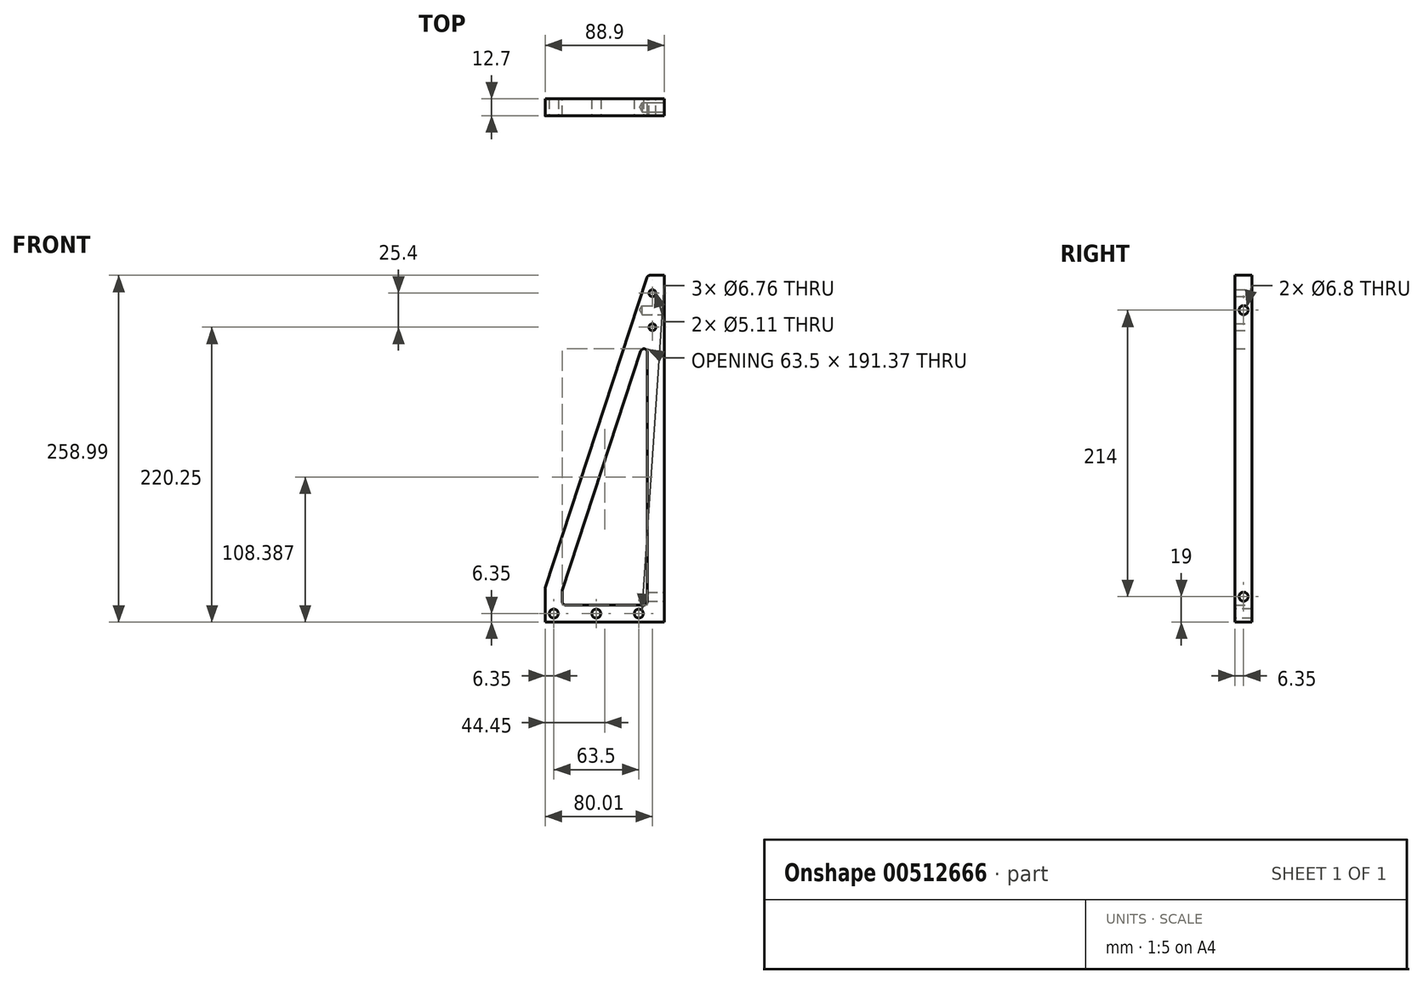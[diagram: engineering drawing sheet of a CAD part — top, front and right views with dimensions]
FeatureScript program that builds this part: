
annotation { "Feature Type Name" : "Feature", "Feature Type Description" : "" }
export const myFeature = defineFeature(function(context is Context, id is Id, definition is map)
    precondition{}
    {
        {
            var Q0;
            Q0=qCreatedBy(makeId("Front.planeOp"),FACE);
            var sketch = newSketch(context, id + "F0", { "sketchPlane" : qUnion([Q0])});
            skLineSegment(sketch, "E0", {"start": v(0, 0) * mm, "end": v(88.9, 0) * mm});
            skLineSegment(sketch, "E1", {"start": v(0, 0) * mm, "end": v(0, 25.4) * mm});
            skLineSegment(sketch, "E2", {"start": v(0, 25.4) * mm, "end": v(74.12, 252) * mm});
            skPoint(sketch, "E3.endSnap0", {"position": v(0, 12.7) * mm});
            skLineSegment(sketch, "E4", {"start": v(12.7, 23.38) * mm, "end": v(12.7, 12.7) * mm});
            skLineSegment(sketch, "E5", {"start": v(88.9, 0) * mm, "end": v(88.9, 252) * mm});
            skLineSegment(sketch, "E6", {"start": v(88.9, 252) * mm, "end": v(74.12, 252) * mm});
            skLineSegment(sketch, "E7", {"start": v(88.9, 252) * mm, "end": v(88.9, 239.3) * mm});
            skLineSegment(sketch, "E8", {"start": v(88.9, 239.3) * mm, "end": v(88.9, 226.6) * mm});
            skLineSegment(sketch, "E9", {"start": v(88.9, 0) * mm, "end": v(88.9, 12.7) * mm});
            skLineSegment(sketch, "E10", {"start": v(88.9, 12.7) * mm, "end": v(12.7, 12.7) * mm});
            skLineSegment(sketch, "E11", {"start": v(70.53, 30.21) * mm, "end": v(72.74, 26.95) * mm});
            skLineSegment(sketch, "E12", {"start": v(88.9, 12.7) * mm, "end": v(76.2, 12.7) * mm});
            skLineSegment(sketch, "E13", {"start": v(76.2, 12.7) * mm, "end": v(76.2, 217.5) * mm});
            skLineSegment(sketch, "E14", {"start": v(12.7, 23.38) * mm, "end": v(76.2, 217.5) * mm});
            skPoint(sketch, "E15.orphan", {"position": v(12.7, 25.4) * mm});
            skLineSegment(sketch, "E16", {"start": v(74.12, 252) * mm, "end": v(76.4, 258.99) * mm});
            skLineSegment(sketch, "E17", {"start": v(88.9, 252) * mm, "end": v(88.9, 258.99) * mm});
            skLineSegment(sketch, "E18", {"start": v(88.9, 258.99) * mm, "end": v(76.4, 258.99) * mm});
            skSolve(sketch);
        }
        {
            var Q0;
            Q0=makeQuery(id+"F0.imprint","IMPRINT",FACE,{"disambiguationData":[TD([[makeQuery(id+"F0.imprint","IMPRINT",EDGE,{"derivedFrom":sQuery(id+"F0.wireOp",EDGE,"E0")}),1.0]])]});
            var Q1;
            Q1=makeQuery(id+"F0.imprint","IMPRINT",FACE,{"disambiguationData":[TD([[makeQuery(id+"F0.imprint","IMPRINT",EDGE,{"derivedFrom":sQuery(id+"F0.wireOp",EDGE,"E6")}),-1.0]])]});
            extrude(context, id + "F1", {"entities" : qUnion([Q0, Q1]), "depth" : 12.7 * mm});
        }
        {
            var Q0;
            Q0=makeQuery(id+"F1.opExtrude","SWEPT_EDGE",EDGE,{"disambiguationData":[OSD([sQuery(id+"F0.wireOp",EDGE,"E2"),sQuery(id+"F0.wireOp",EDGE,"E6")])]});
            var Q1;
            Q1=makeQuery(id+"F1.opExtrude","SWEPT_EDGE",EDGE,{"disambiguationData":[OSD([sQuery(id+"F0.wireOp",EDGE,"E1"),sQuery(id+"F0.wireOp",EDGE,"E2")])]});
            var Q2;
            Q2=makeQuery(id+"F1.opExtrude","SWEPT_EDGE",EDGE,{"disambiguationData":[OSD([sQuery(id+"F0.wireOp",EDGE,"E10"),sQuery(id+"F0.wireOp",EDGE,"E13")])]});
            var Q3;
            Q3=makeQuery(id+"F1.opExtrude","SWEPT_EDGE",EDGE,{"disambiguationData":[OSD([sQuery(id+"F0.wireOp",EDGE,"E4"),sQuery(id+"F0.wireOp",EDGE,"E10")])]});
            var Q4;
            Q4=makeQuery(id+"F1.opExtrude","SWEPT_EDGE",EDGE,{"disambiguationData":[OSD([sQuery(id+"F0.wireOp",EDGE,"E4"),sQuery(id+"F0.wireOp",EDGE,"E14")])]});
            var Q5;
            Q5=makeQuery(id+"F1.opExtrude","SWEPT_EDGE",EDGE,{"disambiguationData":[OSD([sQuery(id+"F0.wireOp",EDGE,"E13"),sQuery(id+"F0.wireOp",EDGE,"E14")])]});
            var Q6;
            Q6=makeQuery(id+"F1.opExtrude","SWEPT_EDGE",EDGE,{"disambiguationData":[OSD([sQuery(id+"F0.wireOp",EDGE,"E16"),sQuery(id+"F0.wireOp",EDGE,"E18")])]});
            fillet(context, id + "F2", {"entities" : qUnion([Q0, Q1, Q2, Q3, Q4, Q5, Q6]), "radius" : 2.54 * mm, "tangentPropagation" : true, "allowEdgeOverflow" : false});
        }
        {
            var Q0;
            Q0=makeQuery(id+"F1.opExtrude","SWEPT_FACE",FACE,{"disambiguationData":[OSD([sQuery(id+"F0.wireOp",EDGE,"E5"),sQuery(id+"F0.wireOp",EDGE,"E7"),sQuery(id+"F0.wireOp",EDGE,"E8"),sQuery(id+"F0.wireOp",EDGE,"E9")])]});
            var sketch = newSketch(context, id + "F3", { "sketchPlane" : qUnion([Q0])});
            skLineSegment(sketch, "E19", {"start": v(-6.35, 0) * mm, "end": v(-6.35, 19) * mm});
            skLineSegment(sketch, "E20", {"start": v(-6.35, 19) * mm, "end": v(-6.35, 233) * mm});
            skSolve(sketch);
        }
        {
            var Q0;
            Q0=sQuery(id+"F3.wireOp",VERTEX,"E20.end");
            var Q1;
            Q1=sQuery(id+"F3.wireOp",VERTEX,"E20.start");
            var Q2;
            Q2=makeQuery(id+"F1.opExtrude","SWEPT_BODY",BODY,{"disambiguationData":[OSD([sQuery(id+"F0.wireOp",EDGE,"E0"),sQuery(id+"F0.wireOp",EDGE,"E1"),sQuery(id+"F0.wireOp",EDGE,"E2"),sQuery(id+"F0.wireOp",EDGE,"E4"),sQuery(id+"F0.wireOp",EDGE,"E5"),sQuery(id+"F0.wireOp",EDGE,"E6"),sQuery(id+"F0.wireOp",EDGE,"E7"),sQuery(id+"F0.wireOp",EDGE,"E8"),sQuery(id+"F0.wireOp",EDGE,"E9"),sQuery(id+"F0.wireOp",EDGE,"E10"),sQuery(id+"F0.wireOp",EDGE,"E13"),sQuery(id+"F0.wireOp",EDGE,"E14")])]});
            hole(context, id + "F4", {"style" : HoleStyle.SIMPLE, "endStyle" : HoleEndStyle.BLIND, "standardTappedOrClearance" : lookupTablePath({ "standard" : "ISO", "engagement" : "75%", "pitch" : "1.25 mm", "size" : "M8", "type" : "Tapped" }), "standardBlindInLast" : lookupTablePath({ "standard" : "ISO", "engagement" : "75%", "pitch" : "1.25 mm", "size" : "M8", "type" : "Tapped" }), "holeDiameter" : 6.8 * mm, "showTappedDepth" : true, "holeDepth" : 16.45 * mm, "isTappedThrough" : true, "tappedDepth" : 12.7 * mm, "tapClearance" : 3, "locations" : qUnion([Q0, Q1]), "scope" : qUnion([Q2]), "majorDiameter" : 8 * mm});
        }
        {
            var Q0;
            Q0=makeQuery(id+"F1.opExtrude","CAP_FACE",FACE,{"disambiguationData":[OSD([sQuery(id+"F0.wireOp",EDGE,"E0"),sQuery(id+"F0.wireOp",EDGE,"E1"),sQuery(id+"F0.wireOp",EDGE,"E2"),sQuery(id+"F0.wireOp",EDGE,"E4"),sQuery(id+"F0.wireOp",EDGE,"E5"),sQuery(id+"F0.wireOp",EDGE,"E6"),sQuery(id+"F0.wireOp",EDGE,"E7"),sQuery(id+"F0.wireOp",EDGE,"E8"),sQuery(id+"F0.wireOp",EDGE,"E9"),sQuery(id+"F0.wireOp",EDGE,"E10"),sQuery(id+"F0.wireOp",EDGE,"E13"),sQuery(id+"F0.wireOp",EDGE,"E14")])],"isStart":true});
            var sketch = newSketch(context, id + "F5", { "sketchPlane" : qUnion([Q0])});
            skLineSegment(sketch, "E21", {"start": v(-88.9, 252) * mm, "end": v(-88.9, 252) * mm});
            skLineSegment(sketch, "E22", {"start": v(0, 0) * mm, "end": v(-6.35, 0) * mm});
            skLineSegment(sketch, "E23", {"start": v(-6.35, 0) * mm, "end": v(-6.35, 6.35) * mm});
            skLineSegment(sketch, "E24", {"start": v(-88.9, 252) * mm, "end": v(-71.12, 252) * mm});
            skLineSegment(sketch, "E25", {"start": v(-71.12, 252) * mm, "end": v(-71.12, 213.9) * mm});
            skLineSegment(sketch, "E26", {"start": v(-71.12, 213.9) * mm, "end": v(-88.9, 213.9) * mm});
            skLineSegment(sketch, "E27", {"start": v(-88.9, 213.9) * mm, "end": v(-88.9, 252) * mm});
            skLineSegment(sketch, "E28", {"start": v(-80, 252) * mm, "end": v(-80, 245.65) * mm});
            skLineSegment(sketch, "E29", {"start": v(-80, 213.9) * mm, "end": v(-80, 220.25) * mm});
            skLineSegment(sketch, "E30", {"start": v(-6.35, 6.35) * mm, "end": v(-76.2, 6.35) * mm});
            skSolve(sketch);
        }
        {
            var Q0;
            Q0=sQuery(id+"F5.wireOp",VERTEX,"E28.end");
            var Q1;
            Q1=sQuery(id+"F5.wireOp",VERTEX,"E29.end");
            var Q2;
            Q2=makeQuery(id+"F1.opExtrude","SWEPT_BODY",BODY,{"disambiguationData":[OSD([sQuery(id+"F0.wireOp",EDGE,"E0"),sQuery(id+"F0.wireOp",EDGE,"E1"),sQuery(id+"F0.wireOp",EDGE,"E2"),sQuery(id+"F0.wireOp",EDGE,"E4"),sQuery(id+"F0.wireOp",EDGE,"E5"),sQuery(id+"F0.wireOp",EDGE,"E6"),sQuery(id+"F0.wireOp",EDGE,"E7"),sQuery(id+"F0.wireOp",EDGE,"E8"),sQuery(id+"F0.wireOp",EDGE,"E9"),sQuery(id+"F0.wireOp",EDGE,"E10"),sQuery(id+"F0.wireOp",EDGE,"E13"),sQuery(id+"F0.wireOp",EDGE,"E14")])]});
            hole(context, id + "F6", {"style" : HoleStyle.SIMPLE, "endStyle" : HoleEndStyle.BLIND, "standardTappedOrClearance" : lookupTablePath({ "standard" : "ANSI", "fit" : "Normal (ASME)", "size" : "#10", "type" : "Clearance" }), "standardBlindInLast" : lookupTablePath({ "fit" : "Free", "standard" : "ANSI", "size" : "#10", "type" : "Clearance" }), "holeDiameter" : 5.1 * mm, "holeDepth" : 12.7 * mm, "isTappedThrough" : true, "tappedDepth" : 12.7 * mm, "tapClearance" : 3, "locations" : qUnion([Q0, Q1]), "scope" : qUnion([Q2])});
        }
        {
            var Q0;
            Q0=makeQuery(id+"F1.opExtrude","CAP_FACE",FACE,{"disambiguationData":[OSD([sQuery(id+"F0.wireOp",EDGE,"E0"),sQuery(id+"F0.wireOp",EDGE,"E1"),sQuery(id+"F0.wireOp",EDGE,"E2"),sQuery(id+"F0.wireOp",EDGE,"E4"),sQuery(id+"F0.wireOp",EDGE,"E5"),sQuery(id+"F0.wireOp",EDGE,"E7"),sQuery(id+"F0.wireOp",EDGE,"E8"),sQuery(id+"F0.wireOp",EDGE,"E9"),sQuery(id+"F0.wireOp",EDGE,"E10"),sQuery(id+"F0.wireOp",EDGE,"E13"),sQuery(id+"F0.wireOp",EDGE,"E14"),sQuery(id+"F0.wireOp",EDGE,"E16"),sQuery(id+"F0.wireOp",EDGE,"E17"),sQuery(id+"F0.wireOp",EDGE,"E18")])],"isStart":false});
            var sketch = newSketch(context, id + "F7", { "sketchPlane" : qUnion([Q0])});
            skLineSegment(sketch, "E31", {"start": v(0, 6.35) * mm, "end": v(6.35, 6.35) * mm});
            skLineSegment(sketch, "E32", {"start": v(6.35, 6.35) * mm, "end": v(69.85, 6.35) * mm});
            skLineSegment(sketch, "E33", {"start": v(6.35, 6.35) * mm, "end": v(38.1, 6.35) * mm});
            skSolve(sketch);
        }
        {
            var Q0;
            Q0=sQuery(id+"F7.wireOp",VERTEX,"E33.start");
            var Q1;
            Q1=sQuery(id+"F7.wireOp",VERTEX,"E33.end");
            var Q2;
            Q2=sQuery(id+"F7.wireOp",VERTEX,"E32.end");
            var Q3;
            Q3=makeQuery(id+"F1.opExtrude","SWEPT_BODY",BODY,{"disambiguationData":[OSD([sQuery(id+"F0.wireOp",EDGE,"E0"),sQuery(id+"F0.wireOp",EDGE,"E1"),sQuery(id+"F0.wireOp",EDGE,"E2"),sQuery(id+"F0.wireOp",EDGE,"E4"),sQuery(id+"F0.wireOp",EDGE,"E5"),sQuery(id+"F0.wireOp",EDGE,"E7"),sQuery(id+"F0.wireOp",EDGE,"E8"),sQuery(id+"F0.wireOp",EDGE,"E9"),sQuery(id+"F0.wireOp",EDGE,"E10"),sQuery(id+"F0.wireOp",EDGE,"E13"),sQuery(id+"F0.wireOp",EDGE,"E14"),sQuery(id+"F0.wireOp",EDGE,"E16"),sQuery(id+"F0.wireOp",EDGE,"E17"),sQuery(id+"F0.wireOp",EDGE,"E18")])]});
            hole(context, id + "F8", {"style" : HoleStyle.SIMPLE, "endStyle" : HoleEndStyle.THROUGH, "standardTappedOrClearance" : lookupTablePath({ "standard" : "ANSI", "fit" : "Normal (ASME)", "size" : "1/4", "type" : "Clearance" }), "standardBlindInLast" : lookupTablePath({ "fit" : "Free", "standard" : "ANSI", "size" : "1/4", "type" : "Clearance" }), "holeDiameter" : 6.76 * mm, "isTappedThrough" : true, "tappedDepth" : 12.7 * mm, "tapClearance" : 3, "locations" : qUnion([Q0, Q1, Q2]), "scope" : qUnion([Q3])});
        }
    });
